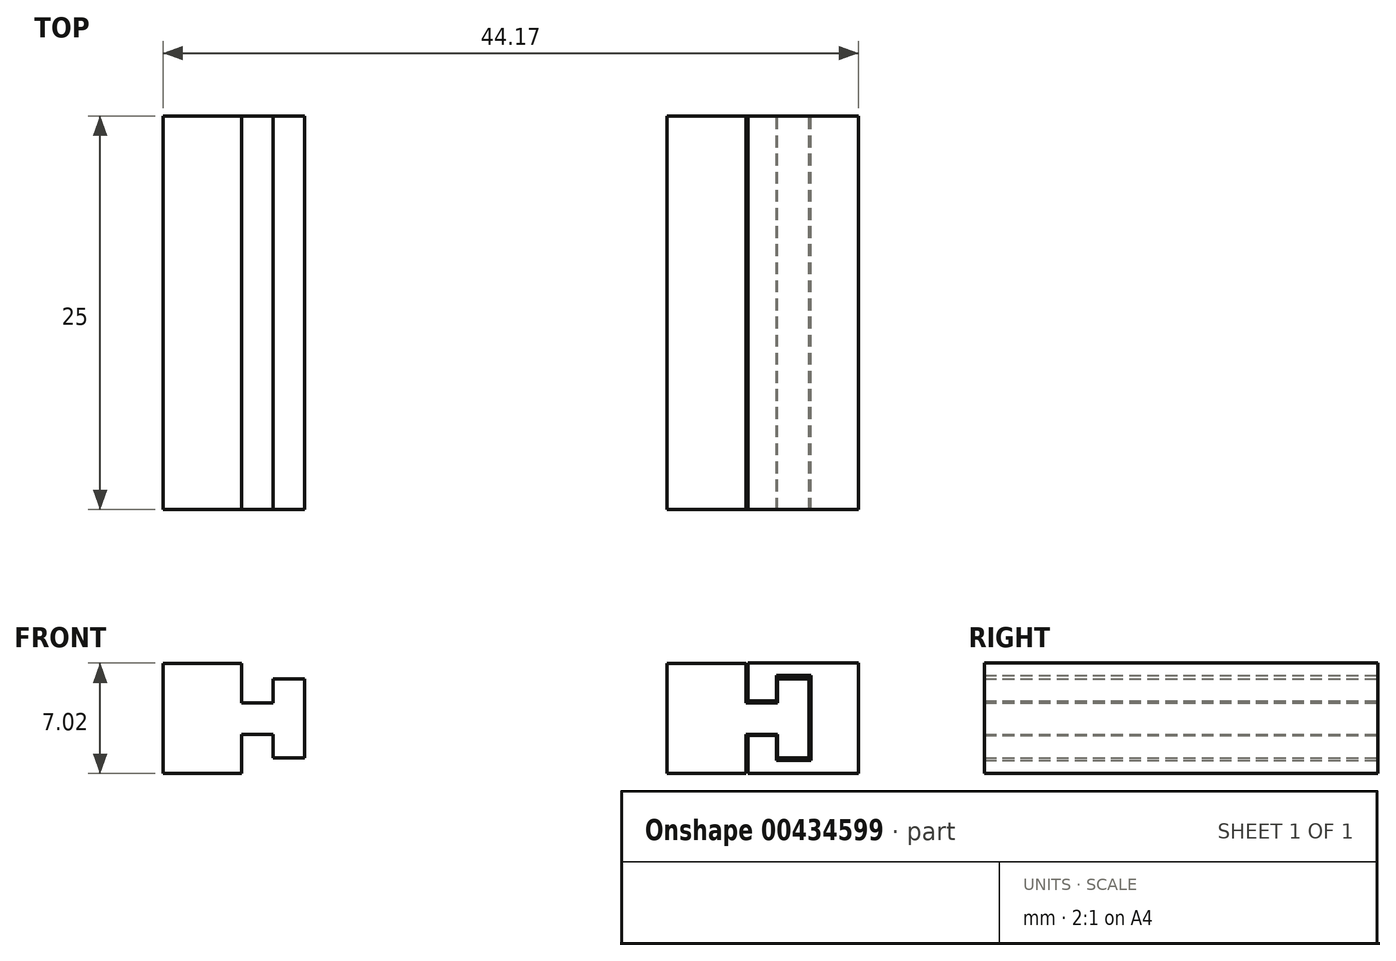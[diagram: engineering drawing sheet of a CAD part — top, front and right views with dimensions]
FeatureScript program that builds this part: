
annotation { "Feature Type Name" : "Feature", "Feature Type Description" : "" }
export const myFeature = defineFeature(function(context is Context, id is Id, definition is map)
    precondition{}
    {
        {
            var Q0;
            Q0=qCreatedBy(makeId("Front.planeOp"),FACE);
            var sketch = newSketch(context, id + "F0", { "sketchPlane" : qUnion([Q0])});
            skLineSegment(sketch, "E0.bottom", {"start": v(-12.7, 0) * mm, "end": v(-17.7, 0) * mm});
            skLineSegment(sketch, "E0.top", {"start": v(-12.7, 7) * mm, "end": v(-17.7, 7) * mm});
            skLineSegment(sketch, "E0.left", {"start": v(-12.7, 0) * mm, "end": v(-12.7, 2.5) * mm});
            skLineSegment(sketch, "E0.right", {"start": v(-17.7, 0) * mm, "end": v(-17.7, 7) * mm});
            skLineSegment(sketch, "E1.bottom", {"start": v(-10.7, 2.5) * mm, "end": v(-12.7, 2.5) * mm});
            skLineSegment(sketch, "E1.top", {"start": v(-10.7, 4.5) * mm, "end": v(-12.7, 4.5) * mm});
            skPoint(sketch, "E1.middle", {"position": v(-11.7, 3.5) * mm});
            skLineSegment(sketch, "E2", {"start": v(-10.7, 4.5) * mm, "end": v(-10.7, 6) * mm});
            skLineSegment(sketch, "E3", {"start": v(-10.7, 2.5) * mm, "end": v(-10.7, 1) * mm});
            skLineSegment(sketch, "E4", {"start": v(-10.7, 1) * mm, "end": v(-8.7, 1) * mm});
            skLineSegment(sketch, "E5", {"start": v(-8.7, 6) * mm, "end": v(-10.7, 6) * mm});
            skLineSegment(sketch, "E6.trimOffspring", {"start": v(-12.7, 4.5) * mm, "end": v(-12.7, 7) * mm});
            skLineSegment(sketch, "E7.bottom", {"start": v(-2.3, 7.32) * mm, "end": v(4.7, 7.32) * mm});
            skLineSegment(sketch, "E7.top", {"start": v(-2.3, 0.32) * mm, "end": v(4.7, 0.32) * mm});
            skLineSegment(sketch, "E7.left", {"start": v(-2.3, 7.32) * mm, "end": v(-2.3, 0.32) * mm});
            skLineSegment(sketch, "E7.right", {"start": v(4.7, 7.32) * mm, "end": v(4.7, 0.32) * mm});
            skPoint(sketch, "E8.positionSnap0", {"position": v(1.2, 0.32) * mm});
            skLineSegment(sketch, "E9", {"start": v(1.2, 7.32) * mm, "end": v(1.2, 0.32) * mm, "construction": true});
            skLineSegment(sketch, "E10", {"start": v(-2.3, 3.82) * mm, "end": v(4.7, 3.82) * mm, "construction": true});
            skPoint(sketch, "E11", {"position": v(-2.3, 3.82) * mm});
            skPoint(sketch, "E12", {"position": v(-17.7, 3.5) * mm});
            skLineSegment(sketch, "E13", {"start": v(-8.7, 6) * mm, "end": v(-8.7, 1) * mm});
            skLineSegment(sketch, "E14.bottom", {"start": v(-0.5, 2.72) * mm, "end": v(-2.3, 2.72) * mm});
            skLineSegment(sketch, "E14.top", {"start": v(-0.5, 4.92) * mm, "end": v(-2.3, 4.92) * mm});
            skPoint(sketch, "E14.middle", {"position": v(-1.4, 3.82) * mm});
            skLineSegment(sketch, "E15", {"start": v(-0.5, 4.92) * mm, "end": v(-0.5, 6.52) * mm});
            skLineSegment(sketch, "E16", {"start": v(-0.5, 2.72) * mm, "end": v(-0.5, 1.12) * mm});
            skLineSegment(sketch, "E17", {"start": v(-0.5, 1.12) * mm, "end": v(1.7, 1.12) * mm});
            skLineSegment(sketch, "E18", {"start": v(1.7, 6.52) * mm, "end": v(-0.5, 6.52) * mm});
            skLineSegment(sketch, "E19", {"start": v(1.7, 6.52) * mm, "end": v(1.7, 1.12) * mm});
            skLineSegment(sketch, "E20", {"start": v(-2.3, 4.92) * mm, "end": v(-2.3, 2.72) * mm, "construction": true});
            skSolve(sketch);
        }
        {
            var Q0;
            Q0=makeQuery(id+"F0.imprint","IMPRINT",FACE,{"disambiguationData":[TD([[makeQuery(id+"F0.imprint","IMPRINT",EDGE,{"derivedFrom":sQuery(id+"F0.wireOp",EDGE,"E0.bottom")}),-1.0]])]});
            var Q1;
            {var subQ2=sQuery(id+"F0.wireOp",EDGE,"E7.bottom");Q1=makeQuery(id+"F0.imprint","IMPRINT",FACE,{"disambiguationData":[TD([[makeQuery(id+"F0.imprint","IMPRINT",EDGE,{"derivedFrom":subQ2}),-1.0]])]});}
            extrude(context, id + "F1", {"entities" : qUnion([Q0, Q1]), "depth" : 25 * mm});
        }
        {
            var Q0;
            Q0=makeQuery(id+"F1.opExtrude","SWEPT_BODY",BODY,{"disambiguationData":[OSD([sQuery(id+"F0.wireOp",EDGE,"E0.bottom"),sQuery(id+"F0.wireOp",EDGE,"E0.top"),sQuery(id+"F0.wireOp",EDGE,"E0.left"),sQuery(id+"F0.wireOp",EDGE,"E0.right"),sQuery(id+"F0.wireOp",EDGE,"E1.bottom"),sQuery(id+"F0.wireOp",EDGE,"E1.top"),sQuery(id+"F0.wireOp",EDGE,"NV92g0XY-ajhz-oQD1-M1nX-0QOLSZXc5US6"),sQuery(id+"F0.wireOp",EDGE,"E3"),sQuery(id+"F0.wireOp",EDGE,"E4"),sQuery(id+"F0.wireOp",EDGE,"h0pm82ZL-Wias-73RV-fyd2-KiAeukKf2Y58"),sQuery(id+"F0.wireOp",EDGE,"E5"),sQuery(id+"F0.wireOp",EDGE,"E6.trimOffspring")])]});
            transform(context, id + "F2", {"entities" : qUnion([Q0]), "transformType" : TransformType.TRANSLATION_3D, "dx" : -21.7 * mm, "dy" : 0 * mm, "dz" : 0 * mm, "makeCopy" : true});
        }
        {
            var Q0;
            Q0=makeQuery(id+"F1.opExtrude","SWEPT_BODY",BODY,{"disambiguationData":[OSD([sQuery(id+"F0.wireOp",EDGE,"E0.bottom"),sQuery(id+"F0.wireOp",EDGE,"E0.top"),sQuery(id+"F0.wireOp",EDGE,"E0.left"),sQuery(id+"F0.wireOp",EDGE,"E0.right"),sQuery(id+"F0.wireOp",EDGE,"E1.bottom"),sQuery(id+"F0.wireOp",EDGE,"E1.top"),sQuery(id+"F0.wireOp",EDGE,"NV92g0XY-ajhz-oQD1-M1nX-0QOLSZXc5US6"),sQuery(id+"F0.wireOp",EDGE,"E3"),sQuery(id+"F0.wireOp",EDGE,"E4"),sQuery(id+"F0.wireOp",EDGE,"h0pm82ZL-Wias-73RV-fyd2-KiAeukKf2Y58"),sQuery(id+"F0.wireOp",EDGE,"E5"),sQuery(id+"F0.wireOp",EDGE,"E6.trimOffspring")])]});
            transform(context, id + "F3", {"entities" : qUnion([Q0]), "transformType" : TransformType.TRANSLATION_3D, "dx" : 10.33 * mm, "dy" : 0 * mm, "dz" : 0 * mm, "makeCopy" : false});
        }
        {
            var Q0;
            Q0=makeQuery(id+"F1.opExtrude","SWEPT_BODY",BODY,{"disambiguationData":[OSD([sQuery(id+"F0.wireOp",EDGE,"E7.bottom"),sQuery(id+"F0.wireOp",EDGE,"E7.top"),sQuery(id+"F0.wireOp",EDGE,"E7.left"),sQuery(id+"F0.wireOp",EDGE,"E7.right"),sQuery(id+"F0.wireOp",EDGE,"E14.bottom"),sQuery(id+"F0.wireOp",EDGE,"E14.top"),sQuery(id+"F0.wireOp",EDGE,"E15"),sQuery(id+"F0.wireOp",EDGE,"E16"),sQuery(id+"F0.wireOp",EDGE,"E17"),sQuery(id+"F0.wireOp",EDGE,"E18"),sQuery(id+"F0.wireOp",EDGE,"E19")])]});
            transform(context, id + "F4", {"entities" : qUnion([Q0]), "transformType" : TransformType.TRANSLATION_3D, "dx" : 0.07 * mm, "dy" : 0 * mm, "dz" : -0.3 * mm, "makeCopy" : false});
        }
    });
